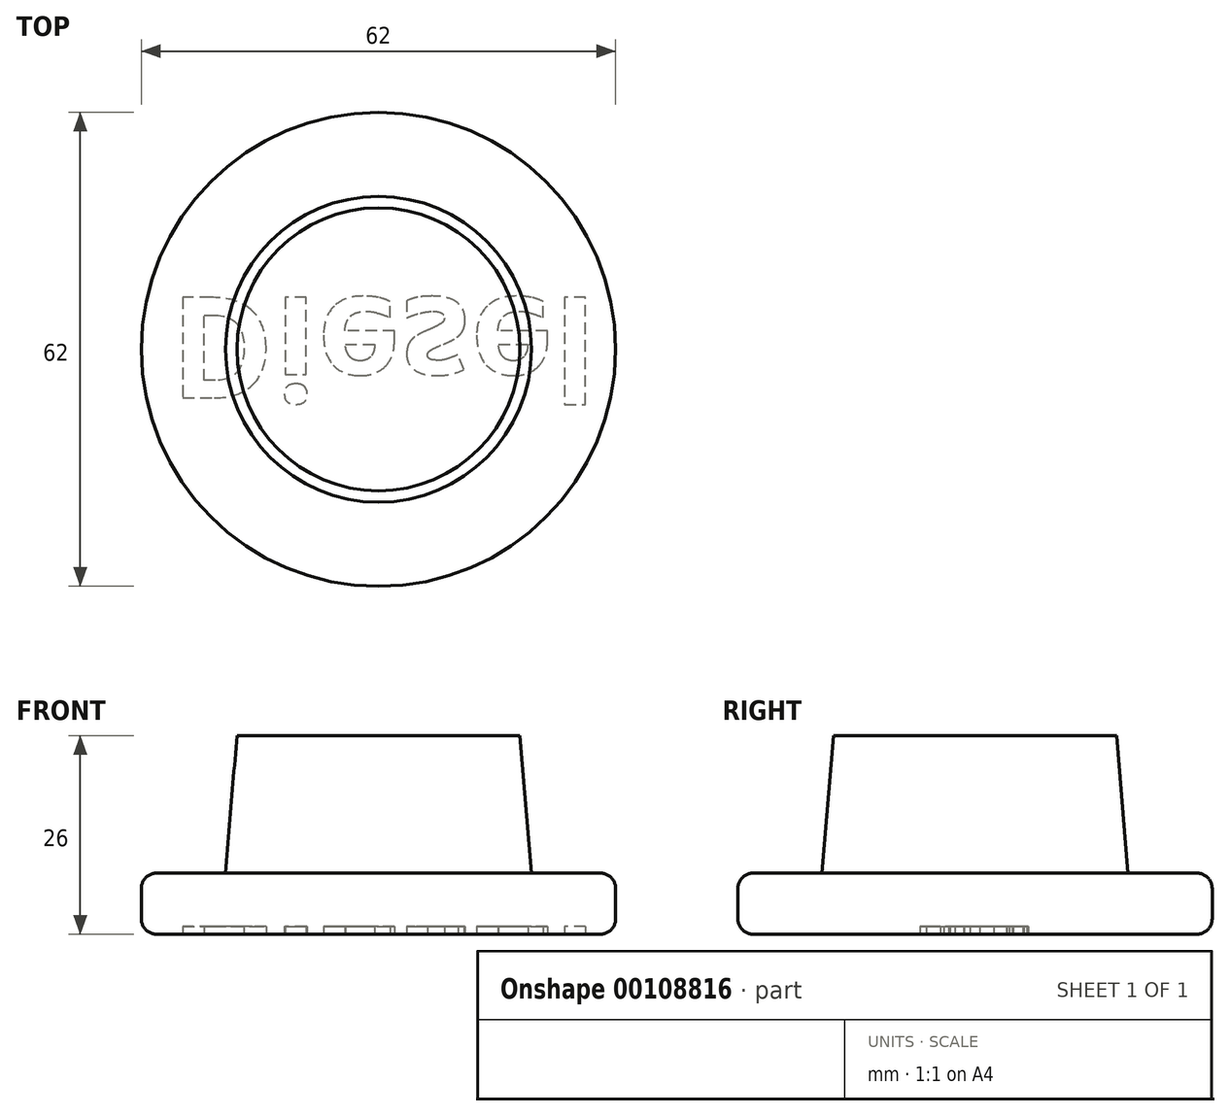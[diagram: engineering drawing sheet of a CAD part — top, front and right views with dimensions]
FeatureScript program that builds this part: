
annotation { "Feature Type Name" : "Feature", "Feature Type Description" : "" }
export const myFeature = defineFeature(function(context is Context, id is Id, definition is map)
    precondition{}
    {
        {
            var Q0;
            Q0=qCreatedBy(makeId("Right.planeOp"),FACE);
            var sketch = newSketch(context, id + "F0", { "sketchPlane" : qUnion([Q0])});
            skLineSegment(sketch, "E0", {"start": v(0, 0) * mm, "end": v(0, 18) * mm});
            skLineSegment(sketch, "E1", {"start": v(0, 18) * mm, "end": v(-20, 18) * mm});
            skLineSegment(sketch, "E2", {"start": v(-20, 18) * mm, "end": v(-18.5, 0) * mm});
            skLineSegment(sketch, "E3", {"start": v(-18.5, 0) * mm, "end": v(0, 0) * mm});
            skSolve(sketch);
        }
        {
            var Q0;
            Q0=makeQuery(id+"F0.imprint","IMPRINT",FACE,{"disambiguationData":[TD([[makeQuery(id+"F0.imprint","IMPRINT",EDGE,{"derivedFrom":sQuery(id+"F0.wireOp",EDGE,"E0")}),1.0]])]});
            var Q1;
            Q1=sQuery(id+"F0.wireOp",EDGE,"E0");
            revolve(context, id + "F1", {"entities" : qUnion([Q0]), "axis" : qUnion([Q1]), "revolveType" : RevolveType.FULL});
        }
        {
            var Q0;
            Q0=makeQuery(id+"F1.opRevolve","SWEPT_FACE",FACE,{"disambiguationData":[OSD([sQuery(id+"F0.wireOp",EDGE,"E1")])]});
            var sketch = newSketch(context, id + "F2", { "sketchPlane" : qUnion([Q0])});
            skCircle(sketch, "E4", {"center": v(0, 0) * mm, "radius": 31 * mm});
            skSolve(sketch);
        }
        {
            var Q0;
            Q0=qSketchRegion(id+"F2",true);
            extrude(context, id + "F3", {"entities" : qUnion([Q0]), "operationType" : NewBodyOperationType.ADD, "depth" : 8 * mm});
        }
        {
            var Q0;
            Q0=makeQuery(id+"F3.opExtrude","CAP_EDGE",EDGE,{"disambiguationData":[OSD([sQuery(id+"F2.wireOp",EDGE,"E4")])],"isStart":false});
            fillet(context, id + "F4", {"entities" : qUnion([Q0]), "radius" : 2 * mm, "tangentPropagation" : true, "allowEdgeOverflow" : false});
        }
        {
            var Q0;
            Q0=makeQuery(id+"F3.opExtrude","CAP_EDGE",EDGE,{"disambiguationData":[OSD([sQuery(id+"F2.wireOp",EDGE,"E4")])],"isStart":true});
            fillet(context, id + "F5", {"entities" : qUnion([Q0]), "radius" : 2 * mm, "tangentPropagation" : true, "allowEdgeOverflow" : false});
        }
        {
            var Q0;
            Q0=makeQuery(id+"F3.opExtrude","CAP_FACE",FACE,{"disambiguationData":[OSD([sQuery(id+"F2.wireOp",EDGE,"E4")])],"isStart":false});
            var sketch = newSketch(context, id + "F6", { "sketchPlane" : qUnion([Q0])});
            skText(sketch, "E5", { "text": "Diesel", "fontName": "OpenSans-Bold.ttf"});
            const initialGuessF6  = {"E5": [-0.02724, -0.00679, 1, 0, 0.01325]};
            skSetInitialGuess(sketch, initialGuessF6);
            skSolve(sketch);
        }
        {
            var Q0;
            Q0=makeQuery(id+"F6.imprint","IMPRINT",FACE,{"disambiguationData":[TD([[makeQuery(id+"F6.imprint","IMPRINT",EDGE,{"derivedFrom":sQuery(id+"F6.wireOp",EDGE,"E5.sketch_text.stroke-12")}),-1.0]])]});
            var Q1;
            Q1=makeQuery(id+"F6.imprint","IMPRINT",FACE,{"disambiguationData":[TD([[makeQuery(id+"F6.imprint","IMPRINT",EDGE,{"derivedFrom":sQuery(id+"F6.wireOp",EDGE,"E5.sketch_text.stroke-17")}),-1.0]])]});
            var Q2;
            Q2=makeQuery(id+"F6.imprint","IMPRINT",FACE,{"disambiguationData":[TD([[makeQuery(id+"F6.imprint","IMPRINT",EDGE,{"derivedFrom":sQuery(id+"F6.wireOp",EDGE,"E5.sketch_text.stroke-41")}),-1.0]])]});
            var Q3;
            Q3=makeQuery(id+"F6.imprint","IMPRINT",FACE,{"disambiguationData":[TD([[makeQuery(id+"F6.imprint","IMPRINT",EDGE,{"derivedFrom":sQuery(id+"F6.wireOp",EDGE,"E5.sketch_text.stroke-87")}),-1.0]])]});
            var Q4;
            Q4=makeQuery(id+"F6.imprint","IMPRINT",FACE,{"disambiguationData":[TD([[makeQuery(id+"F6.imprint","IMPRINT",EDGE,{"derivedFrom":sQuery(id+"F6.wireOp",EDGE,"E5.sketch_text.stroke-0")}),-1.0]])]});
            var Q5;
            Q5=makeQuery(id+"F6.imprint","IMPRINT",FACE,{"disambiguationData":[TD([[makeQuery(id+"F6.imprint","IMPRINT",EDGE,{"derivedFrom":sQuery(id+"F6.wireOp",EDGE,"E5.sketch_text.stroke-21")}),-1.0]])]});
            var Q6;
            Q6=makeQuery(id+"F6.imprint","IMPRINT",FACE,{"disambiguationData":[TD([[makeQuery(id+"F6.imprint","IMPRINT",EDGE,{"derivedFrom":sQuery(id+"F6.wireOp",EDGE,"E5.sketch_text.stroke-67")}),-1.0]])]});
            extrude(context, id + "F7", {"entities" : qUnion([Q0, Q1, Q2, Q3, Q4, Q5, Q6]), "operationType" : NewBodyOperationType.REMOVE, "oppositeDirection" : true, "depth" : 1 * mm});
        }
        {
            var Q0;
            Q0=qCreatedBy(makeId("Top.planeOp"),FACE);
            var sketch = newSketch(context, id + "F8", { "sketchPlane" : qUnion([Q0])});
            skLineSegment(sketch, "E6", {"start": v(-46.57, 0) * mm, "end": v(44.56, 0) * mm});
            skSolve(sketch);
        }
        {
            var Q0;
            Q0=makeQuery(id+"F1.opRevolve","SWEPT_BODY",BODY,{"disambiguationData":[OSD([sQuery(id+"F0.wireOp",EDGE,"E0"),sQuery(id+"F0.wireOp",EDGE,"E1"),sQuery(id+"F0.wireOp",EDGE,"E2"),sQuery(id+"F0.wireOp",EDGE,"E3")])]});
            var Q1;
            Q1=sQuery(id+"F8.wireOp",EDGE,"E6");
            transform(context, id + "F9", {"entities" : qUnion([Q0]), "transformType" : TransformType.ROTATION, "transformAxis" : qUnion([Q1]), "angle" : 180 * degree, "makeCopy" : false});
        }
    });
